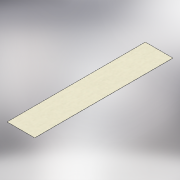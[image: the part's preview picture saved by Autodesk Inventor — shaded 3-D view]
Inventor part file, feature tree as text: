
AUTODESK INVENTOR PART (.ipt)
format: ipt  version: 2017 (Build 210142000, 142)  size: 118,272 bytes
history: native  units: mm
features: extrude x1, sketch x1
ambient origin geometry x8: Origin, YZ Plane, XZ Plane, XY Plane, X Axis, Y Axis, Z Axis, Center Point
bodies: Solide1 (feature_tree)
feature tree (2):
  extrude  "Extrusion1"  Depth=40.0mm
  sketch  "Esquisse1"
